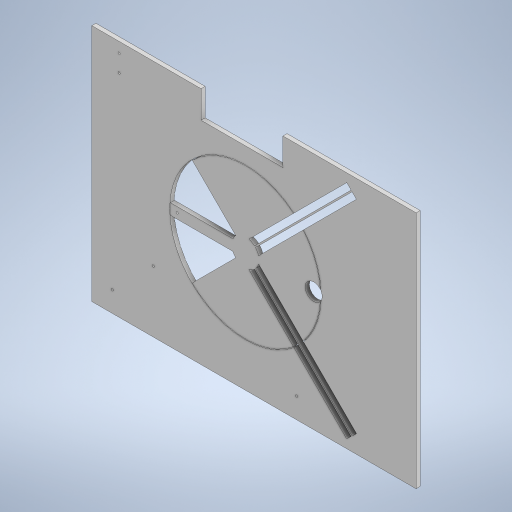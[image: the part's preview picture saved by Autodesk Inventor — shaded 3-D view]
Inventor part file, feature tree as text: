
AUTODESK INVENTOR PART (.ipt)
format: ipt  version: 2023 (Build 270158000, 158)  size: 407,552 bytes
history: native  units: mm
features: extrude x7, sketch x7, other x4, reference x2
ambient origin geometry x8: Origin, YZ Plane, XZ Plane, XY Plane, X Axis, Y Axis, Z Axis, Center Point
bodies: Solid1 (feature_tree)
feature tree (20):
  other  "<userpath>\OneDrive\ClawdDrive\Objet3D\IminaProbe\RoueMDF\Settings.xlsx"
  extrude  "Extrusion1"  Depth=400.0mm
  extrude  "Extrusion2"  TaperAngle=0.0deg  [1 undecoded]
  extrude  "Extrusion3"  Depth=175.0mm
  extrude  "Extrusion4"  Depth=40.0mm
  extrude  "Extrusion5"  Depth=10.0mm
  extrude  "Extrusion6"  Depth=10.0mm
  extrude  "Extrusion7"  Depth=1.0mm
  sketch  "Sketch1"  dims[d0=350.0mm d1=400.0mm]
  sketch  "Sketch2"  dims[d2=6.0mm d3=0.0mm]
  reference  "Reference1"
  sketch  "Sketch3"  dims[d4=175.0mm d5=175.0mm]
  sketch  "Sketch4"  dims[d6=220.0mm d7=40.0mm]
  reference  "Reference5"
  sketch  "Sketch5"  dims[d8=10.0mm d9=10.0mm]
  sketch  "Sketch6"  dims[d10=10.0mm d11=10.0mm]
  sketch  "Sketch7"  dims[d12=1.0mm d13=1.0mm d14=1.0mm d15=1.0mm d16=200.0mm d17=200.0mm d18=222.0mm d19=100.0mm d20=2.25mm d21=2.25mm d22=10.0mm d24=20.0mm d25=0.0mm d26=6.0mm d27=4.0mm d28=4.0mm d29=20.0mm d30=0.0mm d31=3.0mm d32=0.0mm d33=100.0mm d34=6.0mm d35=0.0mm d36=100.0mm d37=25.0mm d38=6.0mm d39=0.0mm d40=40.0mm d41=120.0mm d42=120.0mm d43=6.0mm d44=0.0mm d45=8.0mm d46=8.0mm d47=45.0deg d48=45.0deg d49=10.0mm d50=0.0mm d51=3.0mm d52=15.0mm d53=25.0mm d54=3.0mm d55=40.0mm d56=40.0mm d57=10.0mm d58=0.0mm d59=475.0mm d60=6.0mm d61=0.0mm]
  other  "<userpath>\OneDrive\ClawdDrive\Objet3D\IminaProbe\RoueMDF\Assembly1.iam"
  other  "Assembly1.iam"
  other  "Wheel1:1"
note: 1 required parameter value undecoded (feature->parameter linkage not recoverable at this tier; creation-order binding heuristic only, values carry confidence <= 0.55)
